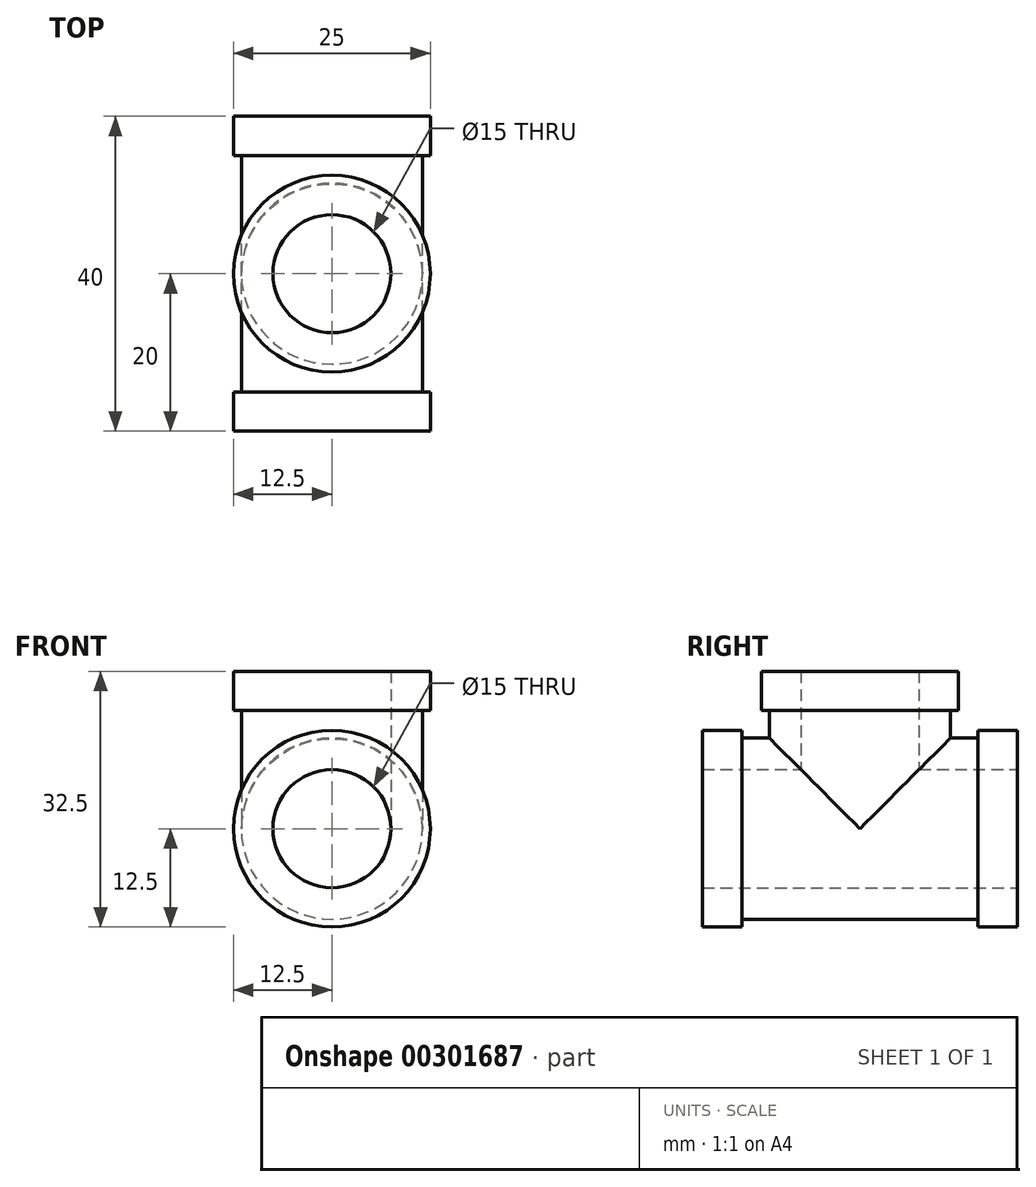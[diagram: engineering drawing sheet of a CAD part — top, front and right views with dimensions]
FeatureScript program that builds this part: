
annotation { "Feature Type Name" : "Feature", "Feature Type Description" : "" }
export const myFeature = defineFeature(function(context is Context, id is Id, definition is map)
    precondition{}
    {
        {
            var Q0;
            Q0=qCreatedBy(makeId("Front.planeOp"),FACE);
            var sketch = newSketch(context, id + "F0", { "sketchPlane" : qUnion([Q0])});
            skCircle(sketch, "E0", {"center": v(0, 0) * mm, "radius": 7.5 * mm});
            skCircle(sketch, "E1", {"center": v(0, 0) * mm, "radius": 11.5 * mm});
            skSolve(sketch);
        }
        {
            var Q0;
            Q0=makeQuery(id+"F0.imprint","IMPRINT",FACE,{"disambiguationData":[TD([[makeQuery(id+"F0.imprint","IMPRINT",EDGE,{"derivedFrom":sQuery(id+"F0.wireOp",EDGE,"E0")}),-1.0]])]});
            extrude(context, id + "F1", {"entities" : qUnion([Q0]), "depth" : 15 * mm});
        }
        {
            var Q0;
            Q0=makeQuery(id+"F1.opExtrude","CAP_FACE",FACE,{"disambiguationData":[OSD([sQuery(id+"F0.wireOp",EDGE,"E0"),sQuery(id+"F0.wireOp",EDGE,"E1")])],"isStart":false});
            var sketch = newSketch(context, id + "F2", { "sketchPlane" : qUnion([Q0])});
            skCircle(sketch, "E2", {"center": v(0, 0) * mm, "radius": 12.5 * mm});
            skCircle(sketch, "E3", {"center": v(0, 0) * mm, "radius": 7.5 * mm});
            skSolve(sketch);
        }
        {
            var Q0;
            Q0=qSketchRegion(id+"F2",true);
            extrude(context, id + "F3", {"entities" : qUnion([Q0]), "operationType" : NewBodyOperationType.ADD, "depth" : 5 * mm});
        }
        {
            var Q0;
            Q0=makeQuery(id+"F1.opExtrude","SWEPT_BODY",BODY,{"disambiguationData":[OSD([sQuery(id+"F0.wireOp",EDGE,"E0"),sQuery(id+"F0.wireOp",EDGE,"E1")])]});
            var Q1;
            Q1=qCreatedBy(makeId("Front.planeOp"),FACE);
            mirror(context, id + "F4", {"operationType" : NewBodyOperationType.ADD, "entities" : qUnion([Q0]), "mirrorPlane" : qUnion([Q1])});
        }
        {
            var Q0;
            Q0=qCreatedBy(makeId("Top.planeOp"),FACE);
            var sketch = newSketch(context, id + "F5", { "sketchPlane" : qUnion([Q0])});
            skCircle(sketch, "E4", {"center": v(0, 0) * mm, "radius": 11.5 * mm});
            skCircle(sketch, "E5", {"center": v(0, 0) * mm, "radius": 7.5 * mm});
            skSolve(sketch);
        }
        {
            var Q0;
            Q0=qSketchRegion(id+"F5",true);
            extrude(context, id + "F6", {"entities" : qUnion([Q0]), "operationType" : NewBodyOperationType.ADD, "depth" : 15 * mm});
        }
        {
            var Q0;
            Q0=makeQuery(id+"F6.opExtrude","CAP_FACE",FACE,{"disambiguationData":[OSD([sQuery(id+"F5.wireOp",EDGE,"E4"),sQuery(id+"F5.wireOp",EDGE,"E5")])],"isStart":false});
            var sketch = newSketch(context, id + "F7", { "sketchPlane" : qUnion([Q0])});
            skCircle(sketch, "E6", {"center": v(0, 0) * mm, "radius": 7.5 * mm});
            skCircle(sketch, "E7", {"center": v(0, 0) * mm, "radius": 12.5 * mm});
            skSolve(sketch);
        }
        {
            var Q0;
            Q0=qSketchRegion(id+"F7",true);
            extrude(context, id + "F8", {"entities" : qUnion([Q0]), "operationType" : NewBodyOperationType.ADD, "depth" : 5 * mm});
        }
        {
            var Q0;
            Q0=makeQuery(id+"F8.opExtrude","CAP_FACE",FACE,{"disambiguationData":[OSD([sQuery(id+"F7.wireOp",EDGE,"E6"),sQuery(id+"F7.wireOp",EDGE,"E7")])],"isStart":false});
            var sketch = newSketch(context, id + "F9", { "sketchPlane" : qUnion([Q0])});
            skCircle(sketch, "E8", {"center": v(0, 0) * mm, "radius": 7.5 * mm});
            skSolve(sketch);
        }
        {
            var Q0;
            Q0=qSketchRegion(id+"F9",true);
            extrude(context, id + "F10", {"entities" : qUnion([Q0]), "operationType" : NewBodyOperationType.REMOVE, "oppositeDirection" : true, "depth" : 20 * mm});
        }
        {
            var Q0;
            Q0=makeQuery(id+"F3.opExtrude","CAP_FACE",FACE,{"disambiguationData":[OSD([sQuery(id+"F2.wireOp",EDGE,"E2"),sQuery(id+"F2.wireOp",EDGE,"E3")])],"isStart":false});
            var sketch = newSketch(context, id + "F11", { "sketchPlane" : qUnion([Q0])});
            skCircle(sketch, "E9", {"center": v(0, 0) * mm, "radius": 7.5 * mm});
            skSolve(sketch);
        }
        {
            var Q0;
            Q0=qSketchRegion(id+"F11",true);
            extrude(context, id + "F12", {"entities" : qUnion([Q0]), "operationType" : NewBodyOperationType.REMOVE, "oppositeDirection" : true, "depth" : 200 * mm});
        }
    });
